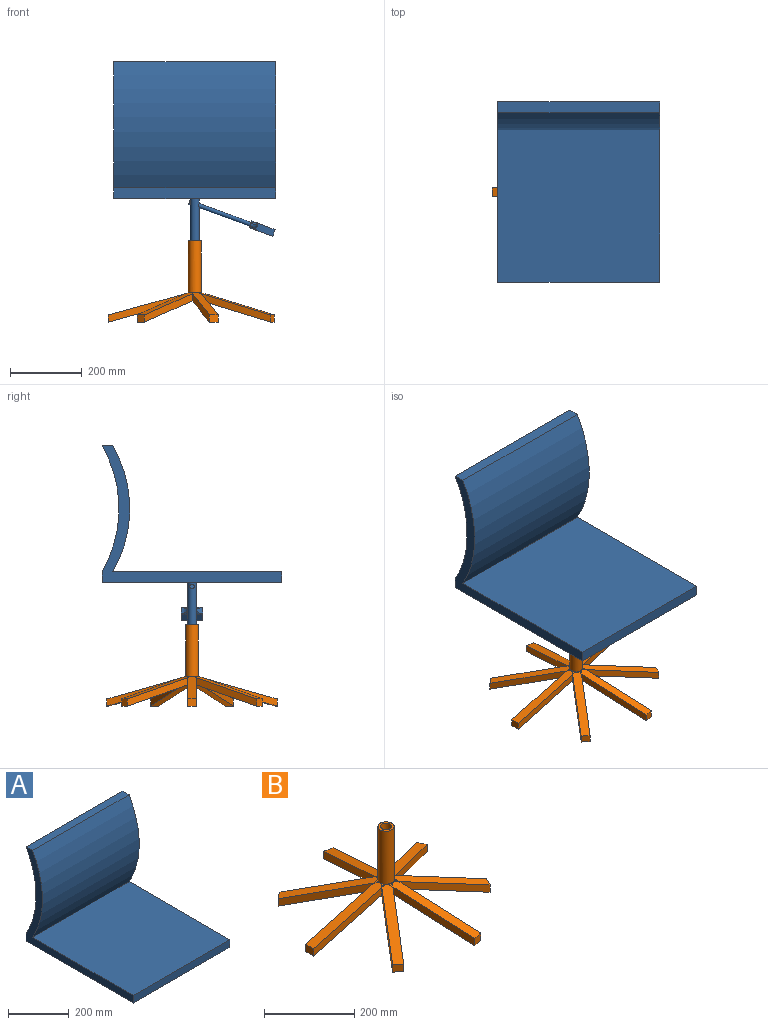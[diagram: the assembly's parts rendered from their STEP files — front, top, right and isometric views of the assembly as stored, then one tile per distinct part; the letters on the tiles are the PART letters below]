
ASSEMBLY  parts=2 mates=1
PART A: 36 faces, bbox 450.2x500.2x580.2 mm
  f0: bspline ~14.67x11.5mm, area 0mm2, adj f5,f26,f33
  f1: bspline ~14.67x10.63mm, area 69.3mm2, adj f21,f28,f35
  f2: bspline ~14.67x10.63mm, area 67.2mm2, adj f21,f28,f30
  f3: bspline ~14.67x11.5mm, area 0mm2, adj f5,f26,f32
  f4: plane 9.4x3.42mm, normal (-0.94,0,0.34), area 5.7mm2, adj f25,f28,f34
  f5: cylinder r=10mm len=21.07mm, axis (-0.94,0,0.34), area 206.6mm2, adj f0,f3,f22,f32,f33
  f6: plane 9.4x3.42mm, normal (-0.94,0,0.34), area 5.7mm2, adj f26,f27,f31
  f7: plane 470x450mm, normal (0,0,1), area 211500mm2, adj f9,f11,f12,f15
  f8: cylinder r=12.5mm len=200mm, axis (0,0,-1), area 15459.7mm2, adj f13,f17,f18,f19,f20
  f9: plane 500x380mm, normal (1,0,0), area 25500mm2, adj f7,f10,f12,f13,f14,f15,f16
  f10: plane 450x30mm, normal (0,1,0), area 13500mm2, adj f9,f11,f13,f14
  f11: plane 500x380mm, normal (-1,0,0), area 25500mm2, adj f7,f10,f12,f13,f14,f15,f16
  f12: plane 450x30mm, normal (0,-1,0), area 13500mm2, adj f7,f9,f11,f13
  f13: plane 500x450mm, normal (0,0,-1), area 224509.1mm2, adj f8,f9,f10,f11,f12
  f14: cylinder r=350mm len=450mm, axis (-1,0,0), area 164933.6mm2, adj f9,f10,f11,f16
  f15: cylinder r=350mm len=450mm, axis (-1,0,0), area 164933.6mm2, adj f7,f9,f11,f16
  f16: plane 450x30mm, normal (0,0,1), area 13500mm2, adj f9,f11,f14,f15
  f17: plane 25x25mm, normal (0,0,-1), area 490.9mm2, adj f8
  f18: plane 12.24x11.43mm, normal (-0.94,0,0.34), area 112.8mm2, adj f8,f19
  f19: cylinder r=6mm len=12.71mm, axis (-0.94,0,0.34), area 109.7mm2, adj f8,f18
  f20: cylinder r=6mm len=148.33mm, axis (-0.94,0,0.34), area 5703.6mm2, adj f8,f22
  f21: cylinder r=10mm len=21.07mm, axis (-0.94,0,0.34), area 206.6mm2, adj f1,f2,f22,f30,f35
  f22: plane 20x18.79mm, normal (-0.94,0,0.34), area 201.1mm2, adj f5,f20,f21,f31,f34
  f23: plane 9.4x3.42mm, normal (-0.94,0,0.34), area 5.7mm2, adj f25,f26,f34
  f24: plane 9.4x3.42mm, normal (-0.94,0,0.34), area 5.7mm2, adj f27,f28,f31
  f25: plane 53.83x35.9mm, normal (0,1,0), area 1000mm2, adj f4,f23,f26,f28,f29
  f26: plane 60.15x47.13mm, normal (0.34,0,0.94), area 3000mm2, adj f0,f3,f6,f23,f25,f27,f29,f32
  f27: plane 53.83x35.9mm, normal (0,-1,0), area 1000mm2, adj f6,f24,f26,f28,f29
  f28: plane 60.15x47.13mm, normal (-0.34,0,-0.94), area 3000mm2, adj f1,f2,f4,f24,f25,f27,f29,f30
  f29: plane 60x18.79mm, normal (0.94,0,-0.34), area 1200mm2, adj f25,f26,f27,f28
  f30: bspline ~23.95x18.94mm, area 167.8mm2, adj f2,f21,f28,f31
  f31: torus R=30mm, axis (0.94,0,-0.34), area 368.7mm2, adj f6,f22,f24,f30,f32
  f32: bspline ~23.88x21.07mm, area 165.7mm2, adj f3,f5,f26,f31
  f33: bspline ~23.95x21.07mm, area 167.8mm2, adj f0,f5,f26,f34
  f34: torus R=30mm, axis (0.94,0,-0.34), area 368.7mm2, adj f4,f22,f23,f33,f35
  f35: bspline ~23.88x18.94mm, area 165.7mm2, adj f1,f21,f28,f34
PART B: 69 faces, bbox 461.2x473x226.2 mm
  f0: plane 167.15x133.29mm, normal (-0.78,-0.62,0), area 4275.7mm2, adj f6,f9,f50,f67
  f1: plane 208.43x79.05mm, normal (-0.97,0.22,0), area 4275.7mm2, adj f10,f12,f51,f52
  f2: plane 10.17x8.11mm, normal (-0.78,-0.62,0), area 8.8mm2, adj f3,f5,f16
  f3: plane 221.9x61.29mm, normal (-0.27,0,0.96), area 5669.1mm2, adj f2,f16,f45,f47,f67,f68
  f4: plane 13x4.69mm, normal (-0.27,0,0.96), area 30.7mm2, adj f5,f7,f16
  f5: plane 10.17x9.74mm, normal (-0.17,0.21,0.96), area 30.7mm2, adj f2,f4,f16
  f6: plane 182.73x152.84mm, normal (-0.17,0.21,0.96), area 5669.1mm2, adj f0,f7,f11,f16,f50,f51
  f7: plane 13x3.59mm, normal (0,1,0), area 8.8mm2, adj f4,f6,f16
  f8: plane 223.53x61.74mm, normal (0.27,0,-0.96), area 5730.6mm2, adj f9,f39,f45,f62,f67,f68
  f9: plane 187.42x155.25mm, normal (0.17,-0.21,-0.96), area 5730.6mm2, adj f0,f8,f10,f50,f51,f62
  f10: plane 222.44x71.95mm, normal (-0.06,-0.26,-0.96), area 5730.6mm2, adj f1,f9,f18,f52,f53,f62
  f11: plane 12.68x3.59mm, normal (-0.97,0.22,0), area 8.8mm2, adj f6,f15,f16
  f12: plane 219.63x71.95mm, normal (0.06,0.26,0.96), area 5669.1mm2, adj f1,f13,f16,f19,f52,f53
  f13: plane 10.17x8.11mm, normal (0.78,0.62,0), area 8.8mm2, adj f12,f14,f16
  f14: plane 10.54x8.11mm, normal (-0.17,0.21,0.96), area 30.7mm2, adj f13,f15,f16
  f15: plane 12.68x5.3mm, normal (0.06,0.26,0.96), area 30.7mm2, adj f11,f14,f16
  f16: cylinder r=18mm len=144.97mm, axis (0,0,-1), area 16322.5mm2, adj f2,f3,f4,f5,f6,f7,f11,f12
  f17: plane 192.62x92.76mm, normal (-0.43,0.9,0), area 4275.7mm2, adj f18,f20,f53,f54
  f18: plane 210.2x115.28mm, normal (-0.24,-0.12,-0.96), area 5730.6mm2, adj f10,f17,f25,f54,f55,f62
  f19: plane 11.72x5.64mm, normal (-0.43,0.9,0), area 8.8mm2, adj f12,f16,f23
  f20: plane 206.36x115.28mm, normal (0.24,0.12,0.96), area 5669.1mm2, adj f16,f17,f21,f26,f54,f55
  f21: plane 12.68x3.59mm, normal (0.97,-0.22,0), area 8.8mm2, adj f16,f20,f22
  f22: plane 12.68x6.74mm, normal (0.06,0.26,0.96), area 30.7mm2, adj f16,f21,f23
  f23: plane 11.72x8.45mm, normal (0.24,0.12,0.96), area 30.7mm2, adj f16,f19,f22
  f24: plane 192.62x92.76mm, normal (0.43,0.9,0), area 4275.7mm2, adj f25,f27,f55,f56
  f25: plane 210.2x115.28mm, normal (-0.24,0.12,-0.96), area 5730.6mm2, adj f18,f24,f32,f56,f57,f62
  f26: plane 11.72x5.64mm, normal (0.43,0.9,0), area 8.8mm2, adj f16,f20,f30
  f27: plane 206.36x115.28mm, normal (0.24,-0.12,0.96), area 5669.1mm2, adj f16,f24,f28,f33,f56,f57
  f28: plane 11.72x5.64mm, normal (0.43,-0.9,0), area 8.8mm2, adj f16,f27,f29
  f29: plane 11.72x5.64mm, normal (0.24,0.12,0.96), area 30.7mm2, adj f16,f28,f30
  f30: plane 11.72x5.64mm, normal (0.24,-0.12,0.96), area 30.7mm2, adj f16,f26,f29
  f31: plane 208.43x79.05mm, normal (0.97,0.22,0), area 4275.7mm2, adj f32,f34,f57,f58
  f32: plane 222.44x71.95mm, normal (-0.06,0.26,-0.96), area 5730.6mm2, adj f25,f31,f39,f58,f59,f62
  f33: plane 12.68x3.59mm, normal (0.97,0.22,0), area 8.8mm2, adj f16,f27,f37
  f34: plane 219.63x71.95mm, normal (0.06,-0.26,0.96), area 5669.1mm2, adj f16,f31,f35,f40,f58,f59
  f35: plane 11.72x5.64mm, normal (-0.43,-0.9,0), area 8.8mm2, adj f16,f34,f36
  f36: plane 11.72x8.45mm, normal (0.24,-0.12,0.96), area 30.7mm2, adj f16,f35,f37
  f37: plane 12.68x6.74mm, normal (0.06,-0.26,0.96), area 30.7mm2, adj f16,f33,f36
  f38: plane 167.15x133.29mm, normal (0.78,-0.62,0), area 4275.7mm2, adj f39,f41,f59,f60
  f39: plane 187.42x155.25mm, normal (0.17,0.21,-0.96), area 5730.6mm2, adj f8,f32,f38,f60,f61,f62
  f40: plane 10.17x8.11mm, normal (0.78,-0.62,0), area 8.8mm2, adj f16,f34,f44
  f41: plane 182.73x152.84mm, normal (-0.17,-0.21,0.96), area 5669.1mm2, adj f16,f38,f42,f46,f60,f61
  f42: plane 12.68x3.59mm, normal (-0.97,-0.22,0), area 8.8mm2, adj f16,f41,f43
  f43: plane 12.68x5.3mm, normal (0.06,-0.26,0.96), area 30.7mm2, adj f16,f42,f44
  f44: plane 10.54x8.11mm, normal (-0.17,-0.21,0.96), area 30.7mm2, adj f16,f40,f43
  f45: plane 213.79x79.05mm, normal (0,-1,0), area 4275.7mm2, adj f3,f8,f61,f68
  f46: plane 13x3.59mm, normal (0,-1,0), area 8.8mm2, adj f16,f41,f49
  f47: plane 10.17x8.11mm, normal (-0.78,0.62,0), area 8.8mm2, adj f3,f16,f48
  f48: plane 10.17x9.74mm, normal (-0.17,-0.21,0.96), area 30.7mm2, adj f16,f47,f49
  f49: plane 13x4.69mm, normal (-0.27,0,0.96), area 30.7mm2, adj f16,f46,f48
  f50: plane 20x19.55mm, normal (-0.62,0.78,0), area 500mm2, adj f0,f6,f9,f51
  f51: plane 167.15x133.29mm, normal (0.78,0.62,0), area 4275.7mm2, adj f1,f6,f9,f50
  f52: plane 24.37x20mm, normal (0.22,0.97,0), area 500mm2, adj f1,f10,f12,f53
  f53: plane 208.43x79.05mm, normal (0.97,-0.22,0), area 4275.7mm2, adj f10,f12,f17,f52
  f54: plane 22.52x20mm, normal (0.9,0.43,0), area 500mm2, adj f17,f18,f20,f55
  f55: plane 192.62x92.76mm, normal (0.43,-0.9,0), area 4275.7mm2, adj f18,f20,f24,f54
  f56: plane 22.52x20mm, normal (0.9,-0.43,0), area 500mm2, adj f24,f25,f27,f57
  f57: plane 192.62x92.76mm, normal (-0.43,-0.9,0), area 4275.7mm2, adj f25,f27,f31,f56
  f58: plane 24.37x20mm, normal (0.22,-0.97,0), area 500mm2, adj f31,f32,f34,f59
  f59: plane 208.43x79.05mm, normal (-0.97,-0.22,0), area 4275.7mm2, adj f32,f34,f38,f58
  f60: plane 20x19.55mm, normal (-0.62,-0.78,0), area 500mm2, adj f38,f39,f41,f61
  f61: plane 167.15x133.29mm, normal (-0.78,0.62,0), area 4275.7mm2, adj f39,f41,f45,f60
  f62: cylinder r=18mm len=36mm, axis (0,0,-1), area 21.8mm2, adj f8,f9,f10,f18,f25,f32,f39,f66
  f63: plane 36x36mm, normal (0,0,1), area 527mm2, adj f16,f64
  f64: cylinder r=12.5mm len=130mm, axis (0,0,1), area 10210.2mm2, adj f63,f65
  f65: plane 25x25mm, normal (0,0,1), area 490.9mm2, adj f64
  f66: plane 36x36mm, normal (0,0,-1), area 1017.9mm2, adj f62
  f67: plane 213.79x79.05mm, normal (0,1,0), area 4275.7mm2, adj f0,f3,f8,f68
  f68: plane 25x20mm, normal (-1,0,0), area 500mm2, adj f3,f8,f45,f67
PLACE A t=(-25.08,121.67,207.49)mm
PLACE B t=(-25.08,121.67,0)mm
MATE slider A.f8 <-> B.f16  axis (0,0,-1) through (-25.08,121.67,57.49)mm
